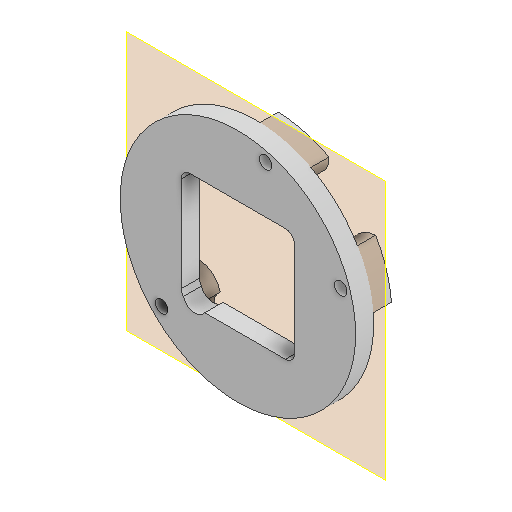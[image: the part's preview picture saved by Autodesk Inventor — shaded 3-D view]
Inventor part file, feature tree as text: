
AUTODESK INVENTOR PART (.ipt)
format: ipt  version: 2022 (Build 260153000, 153)  size: 217,600 bytes
history: native  units: in
note: dims shown in document units (in); Inventor stores cm internally (conversion verified against a paired STEP export)
features: reference x11, other x11, sketch x5, extrude x4, projected_geometry x2, plane x1, hole x1
ambient origin geometry x8: Origin, YZ Plane, XZ Plane, XY Plane, X Axis, Y Axis, Z Axis, Center Point
bodies: Solid1 (feature_tree)
feature tree (35):
  plane  "Work Plane1"
  extrude  "Extrusion1"  Depth=0.9843in
  hole  "Bohrung1"  [1 undecoded]
  extrude  "Extrusion4"  Depth=0.2362in
  extrude  "Extrusion5"  Depth=0.315in
  extrude  "Extrusion6"  Depth=0.315in
  sketch  "Sketch1"  dims[d0=0.1575in d1=0.0in]
  reference  "Reference1"
  reference  "Reference5"
  reference  "Reference6"
  reference  "Reference7"
  sketch  "Skizze4"  dims[d9=0.1102in d10=0.75in d11=0.2559in d12=0.2165in d13=0.5635in d14=1.0in d15=0.8108in d17=0.9843in]
  reference  "Referenz9"
  sketch  "Skizze6"  dims[d18=0.9843in d19=0.0787in]
  projected_geometry  "Projizierte Kontur1"
  sketch  "Skizze7"  dims[d20=0.2362in d21=0.2362in]
  projected_geometry  "Projizierte Kontur2"
  sketch  "Skizze8"  dims[d22=0.1575in d23=0.0in d24=0.315in d25=0.315in d26=0.315in d27=0.1181in d28=0.0in d29=1.5748in d30=0.0197in d31=0.0197in d32=0.0197in d33=0.0197in d34=0.0197in d35=0.0197in d36=0.3937in d37=0.0in]
  reference  "Referenz10"
  reference  "Referenz11"
  reference  "Referenz12"
  reference  "Referenz13"
  reference  "Referenz14"
  reference  "Referenz15"
  other  "<userpath>\Documents\Matchboxscope\INVENTOR\Matchboxscope_v1.iam"
  other  "Matchboxscope_v1.iam"
  other  "Matchboxscope_middle2_v1:1"
  other  "Matchboxscope_middle2_v2:1"
  other  "Anglerfish_lunchbox_m12large_flipped_v0.iam"
  other  "DIN 912 - replaced by DIN EN ISO 4762 M3 x 12:7"
  other  "DIN 912 - replaced by DIN EN ISO 4762 M3 x 12:5"
  other  "DIN 912 - replaced by DIN EN ISO 4762 M3 x 12:1"
  other  "DIN 912 - replaced by DIN EN ISO 4762 M3 x 12:6"
  other  "DIN 912 - replaced by DIN EN ISO 4762 M3 x 12:2"
  other  "DIN 912 - replaced by DIN EN ISO 4762 M3 x 12:4"
note: 1 required parameter value undecoded (feature->parameter linkage not recoverable at this tier; creation-order binding heuristic only, values carry confidence <= 0.55)
